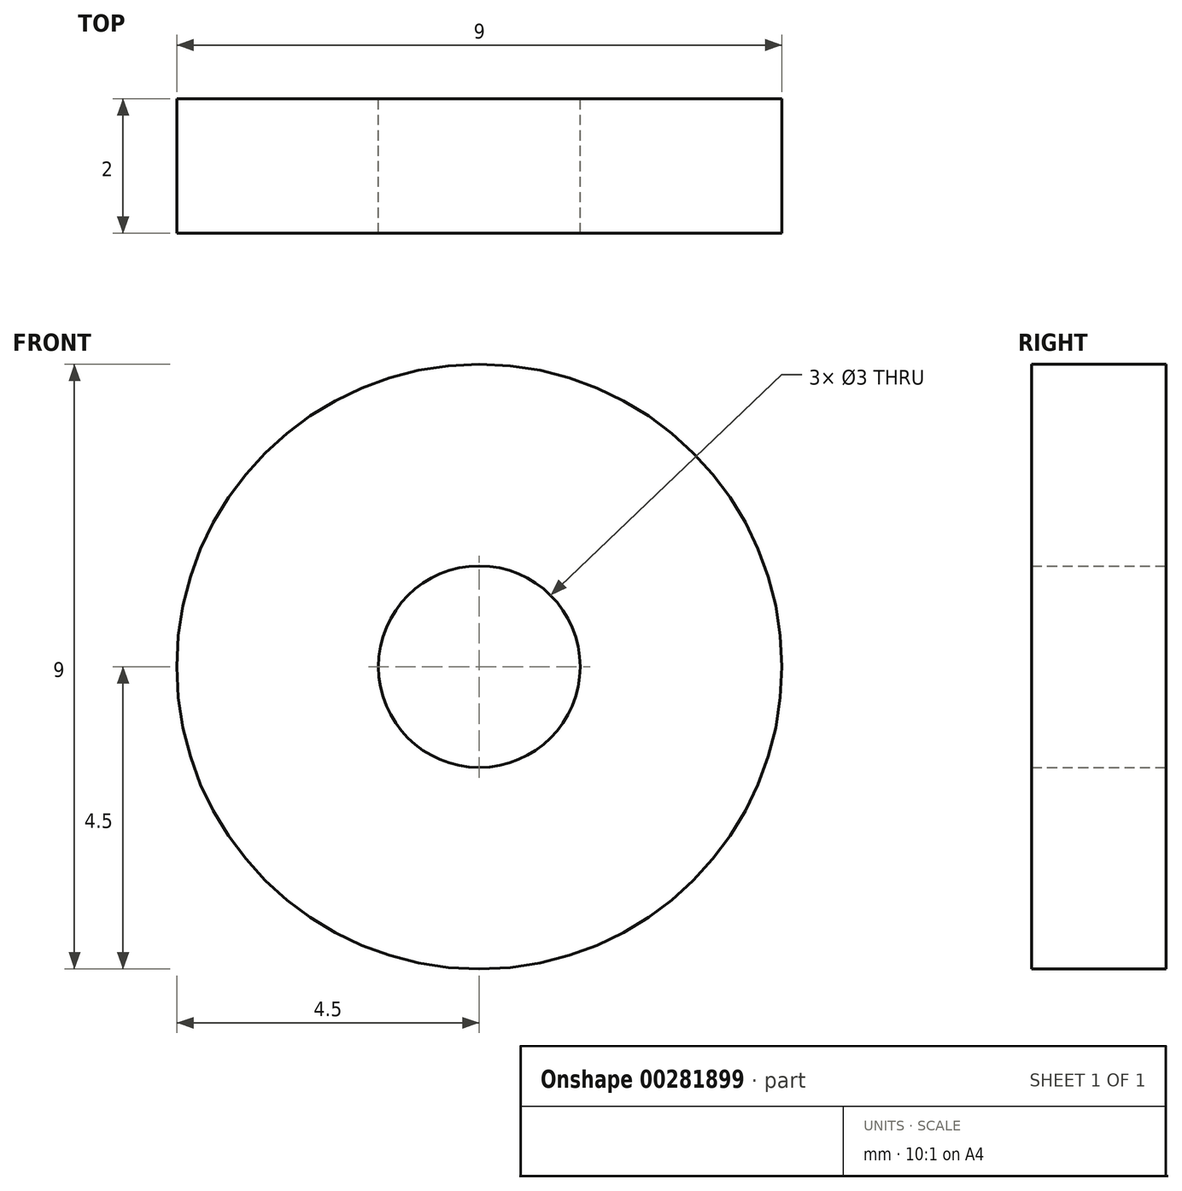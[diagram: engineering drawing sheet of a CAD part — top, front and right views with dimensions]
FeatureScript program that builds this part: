
annotation { "Feature Type Name" : "Feature", "Feature Type Description" : "" }
export const myFeature = defineFeature(function(context is Context, id is Id, definition is map)
    precondition{}
    {
        {
            var Q0;
            Q0=qCreatedBy(makeId("Front.planeOp"),FACE);
            var sketch = newSketch(context, id + "F0", { "sketchPlane" : qUnion([Q0])});
            skCircle(sketch, "E0", {"center": v(0, 0) * mm, "radius": 1.5 * mm});
            skCircle(sketch, "E1", {"center": v(0, 0) * mm, "radius": 4.5 * mm});
            skSolve(sketch);
        }
        {
            var Q0;
            Q0=qSketchRegion(id+"F0",true);
            extrude(context, id + "F1", {"entities" : qUnion([Q0]), "depth" : 2 * mm});
        }
    });
